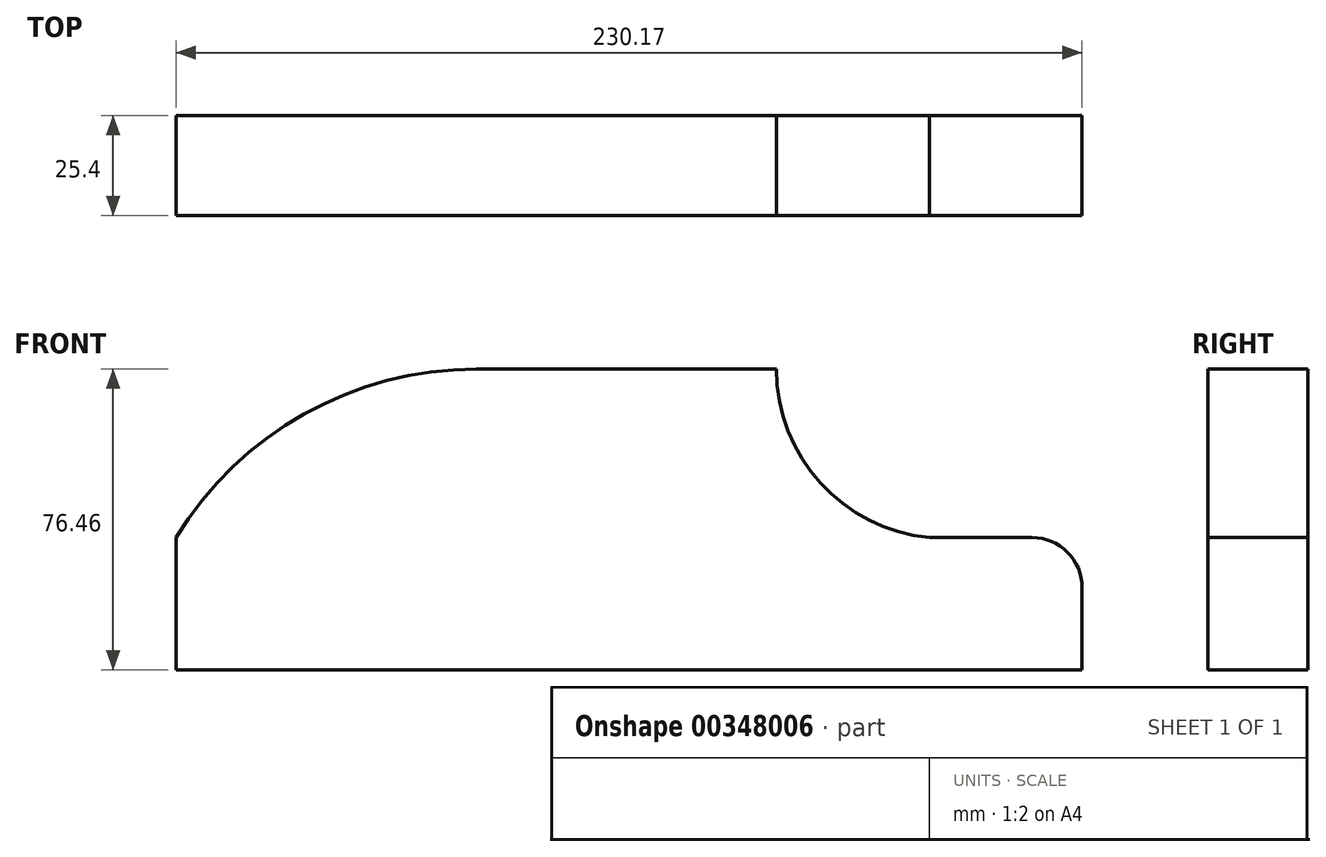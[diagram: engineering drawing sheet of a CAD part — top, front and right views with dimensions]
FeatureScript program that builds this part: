
annotation { "Feature Type Name" : "Feature", "Feature Type Description" : "" }
export const myFeature = defineFeature(function(context is Context, id is Id, definition is map)
    precondition{}
    {
        {
            var Q0;
            Q0=qCreatedBy(makeId("Front.planeOp"),FACE);
            var sketch = newSketch(context, id + "F0", { "sketchPlane" : qUnion([Q0])});
            skLineSegment(sketch, "E0.bottom", {"start": v(0, 0) * mm, "end": v(-76.26, 0) * mm});
            skLineSegment(sketch, "E0.top", {"start": v(0, 33.62) * mm, "end": v(-76.26, 33.62) * mm});
            skLineSegment(sketch, "E0.left", {"start": v(0, 0) * mm, "end": v(0, 33.62) * mm});
            skLineSegment(sketch, "E0.right", {"start": v(-76.26, 0) * mm, "end": v(-76.26, 33.62) * mm});
            skLineSegment(sketch, "E1.bottom", {"start": v(0, 33.62) * mm, "end": v(76.23, 33.62) * mm});
            skLineSegment(sketch, "E1.top", {"start": v(0, 0) * mm, "end": v(76.23, 0) * mm});
            skLineSegment(sketch, "E1.left", {"start": v(0, 33.62) * mm, "end": v(0, 0) * mm});
            skLineSegment(sketch, "E1.right", {"start": v(76.23, 33.62) * mm, "end": v(76.23, 0) * mm});
            skLineSegment(sketch, "E2.bottom", {"start": v(76.23, 33.62) * mm, "end": v(153.9, 33.62) * mm});
            skLineSegment(sketch, "E2.top", {"start": v(76.23, 0) * mm, "end": v(153.9, 0) * mm});
            skLineSegment(sketch, "E2.right", {"start": v(153.9, 33.62) * mm, "end": v(153.9, 0) * mm});
            skLineSegment(sketch, "E3.top", {"start": v(0, 76.46) * mm, "end": v(76.23, 76.46) * mm});
            skLineSegment(sketch, "E3.left", {"start": v(0, 33.62) * mm, "end": v(0, 76.46) * mm});
            skLineSegment(sketch, "E3.right", {"start": v(76.23, 33.62) * mm, "end": v(76.23, 76.46) * mm});
            skArc(sketch, "E4", {"start": v(0, 76.46) * mm, "mid": v(-43.74, 65.02) * mm, "end": v(-76.26, 33.62) * mm});
            skArc(sketch, "E5", {"start": v(76.23, 76.46) * mm, "mid": v(87.39, 47.55) * mm, "end": v(115.07, 33.62) * mm});
            skSolve(sketch);
        }
        {
            var Q0;
            Q0=makeQuery(id+"F0.imprint","IMPRINT",FACE,{"disambiguationData":[TD([[makeQuery(id+"F0.imprint","IMPRINT",EDGE,{"derivedFrom":sQuery(id+"F0.wireOp",EDGE,"E0.top")}),-1.0]])]});
            var Q1;
            Q1=makeQuery(id+"F0.imprint","IMPRINT",FACE,{"disambiguationData":[TD([[makeQuery(id+"F0.imprint","IMPRINT",EDGE,{"derivedFrom":sQuery(id+"F0.wireOp",EDGE,"E0.bottom")}),-1.0]])]});
            var Q2;
            Q2=makeQuery(id+"F0.imprint","IMPRINT",FACE,{"disambiguationData":[TD([[makeQuery(id+"F0.imprint","IMPRINT",EDGE,{"derivedFrom":sQuery(id+"F0.wireOp",EDGE,"E1.top")}),1.0]])]});
            var Q3;
            Q3=makeQuery(id+"F0.imprint","IMPRINT",FACE,{"disambiguationData":[TD([[makeQuery(id+"F0.imprint","IMPRINT",EDGE,{"derivedFrom":sQuery(id+"F0.wireOp",EDGE,"E1.bottom")}),1.0]])]});
            var Q4;
            Q4=makeQuery(id+"F0.imprint","IMPRINT",FACE,{"disambiguationData":[TD([[makeQuery(id+"F0.imprint","IMPRINT",EDGE,{"derivedFrom":sQuery(id+"F0.wireOp",EDGE,"E2.top")}),1.0]])]});
            var Q5;
            {var subQ0=sQuery(id+"F0.wireOp",EDGE,"E3.right");Q5=makeQuery(id+"F0.imprint","IMPRINT",FACE,{"disambiguationData":[TD([[makeQuery(id+"F0.imprint","IMPRINT",EDGE,{"derivedFrom":subQ0}),-1.0]])]});}
            extrude(context, id + "F1", {"entities" : qUnion([Q0, Q1, Q2, Q3, Q4, Q5]), "depth" : 25.4 * mm});
        }
        {
            var Q0;
            Q0=makeQuery(id+"F1.opExtrude","SWEPT_EDGE",EDGE,{"disambiguationData":[OSD([sQuery(id+"F0.wireOp",EDGE,"E2.bottom"),sQuery(id+"F0.wireOp",EDGE,"E2.right")])]});
            fillet(context, id + "F2", {"entities" : qUnion([Q0]), "radius" : 12.7 * mm, "tangentPropagation" : true, "allowEdgeOverflow" : false});
        }
    });
